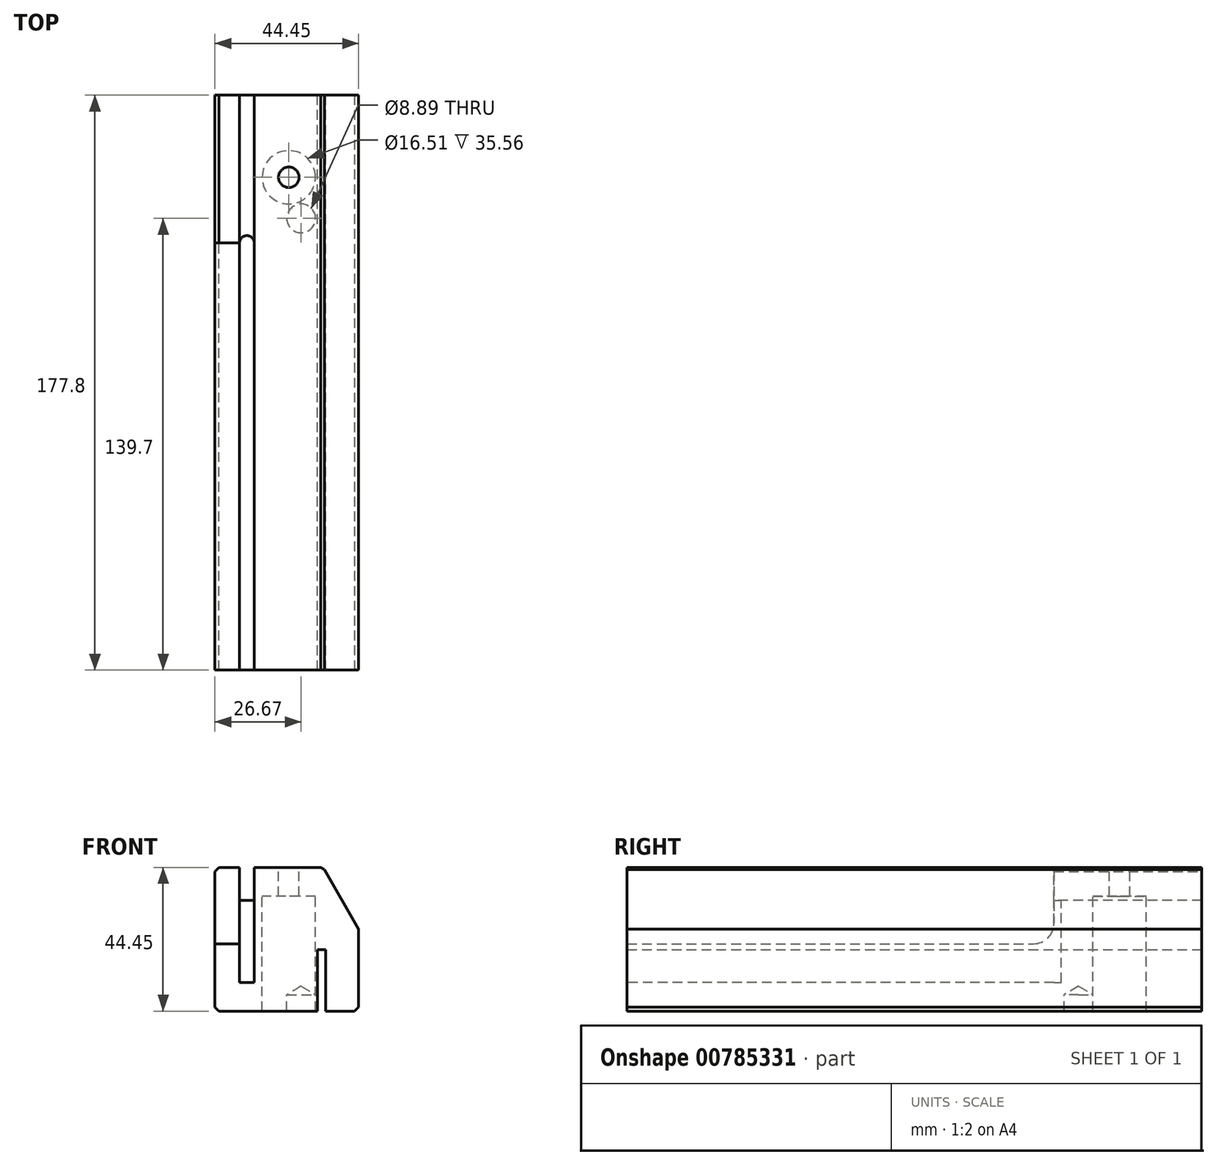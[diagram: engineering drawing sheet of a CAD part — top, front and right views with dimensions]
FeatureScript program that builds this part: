
annotation { "Feature Type Name" : "Feature", "Feature Type Description" : "" }
export const myFeature = defineFeature(function(context is Context, id is Id, definition is map)
    precondition{}
    {
        {
            var Q0;
            Q0=qCreatedBy(makeId("Front.planeOp"),FACE);
            var sketch = newSketch(context, id + "F0", { "sketchPlane" : qUnion([Q0])});
            skLineSegment(sketch, "E0", {"start": v(0, 0) * mm, "end": v(0, 44.45) * mm});
            skLineSegment(sketch, "E1", {"start": v(0, 44.45) * mm, "end": v(33.45, 44.45) * mm});
            skLineSegment(sketch, "E2", {"start": v(33.45, 44.45) * mm, "end": v(44.45, 25.4) * mm});
            skLineSegment(sketch, "E3", {"start": v(44.45, 25.4) * mm, "end": v(44.45, 0) * mm});
            skLineSegment(sketch, "E4.bottom", {"start": v(34.3, 19.05) * mm, "end": v(31.75, 19.05) * mm});
            skLineSegment(sketch, "E4.left", {"start": v(34.3, 19.05) * mm, "end": v(34.3, 0) * mm});
            skLineSegment(sketch, "E4.right", {"start": v(31.75, 19.05) * mm, "end": v(31.75, 0) * mm});
            skLineSegment(sketch, "E5", {"start": v(0, 0) * mm, "end": v(31.75, 0) * mm});
            skLineSegment(sketch, "E6", {"start": v(34.3, 0) * mm, "end": v(44.45, 0) * mm});
            skSolve(sketch);
        }
        {
            var Q0;
            Q0=makeQuery(id+"F0.imprint","IMPRINT",FACE,{"disambiguationData":[TD([[makeQuery(id+"F0.imprint","IMPRINT",EDGE,{"derivedFrom":sQuery(id+"F0.wireOp",EDGE,"E0")}),-1.0]])]});
            extrude(context, id + "F1", {"entities" : qUnion([Q0]), "depth" : 177.8 * mm, "offsetDistance" : 25.4 * mm});
        }
        {
            var Q0;
            Q0=makeQuery(id+"F1.opExtrude","SWEPT_FACE",FACE,{"disambiguationData":[OSD([sQuery(id+"F0.wireOp",EDGE,"E0")])]});
            var sketch = newSketch(context, id + "F2", { "sketchPlane" : qUnion([Q0])});
            skLineSegment(sketch, "E7.bottom", {"start": v(177.8, 44.45) * mm, "end": v(45.72, 44.45) * mm});
            skLineSegment(sketch, "E7.top", {"start": v(177.8, 20.83) * mm, "end": v(52.07, 20.83) * mm});
            skLineSegment(sketch, "E7.left", {"start": v(177.8, 44.45) * mm, "end": v(177.8, 20.83) * mm});
            skLineSegment(sketch, "E7.right", {"start": v(45.72, 44.45) * mm, "end": v(45.72, 27.18) * mm});
            skPoint(sketch, "E8.visualSharp", {"position": v(45.72, 20.83) * mm});
            skArc(sketch, "E8.filletArc", {"start": v(45.72, 27.18) * mm, "mid": v(47.58, 22.69) * mm, "end": v(52.07, 20.83) * mm});
            skSolve(sketch);
        }
        {
            var Q0;
            Q0=makeQuery(id+"F2.imprint","IMPRINT",FACE,{"disambiguationData":[TD([[makeQuery(id+"F2.imprint","IMPRINT",EDGE,{"derivedFrom":sQuery(id+"F2.wireOp",EDGE,"E7.bottom")}),1.0]])]});
            extrude(context, id + "F3", {"entities" : qUnion([Q0]), "operationType" : NewBodyOperationType.REMOVE, "oppositeDirection" : true, "depth" : 9.9 * mm, "offsetDistance" : 25.4 * mm});
        }
        {
            var Q0;
            Q0=makeQuery(id+"F1.opExtrude","SWEPT_FACE",FACE,{"disambiguationData":[OSD([sQuery(id+"F0.wireOp",EDGE,"E1")])]});
            var sketch = newSketch(context, id + "F4", { "sketchPlane" : qUnion([Q0])});
            skLineSegment(sketch, "E9.bottom", {"start": v(7.62, 0) * mm, "end": v(12.2, 0) * mm});
            skLineSegment(sketch, "E9.top", {"start": v(7.62, -177.8) * mm, "end": v(12.2, -177.8) * mm});
            skLineSegment(sketch, "E9.left", {"start": v(7.62, 0) * mm, "end": v(7.62, -177.8) * mm});
            skLineSegment(sketch, "E9.right", {"start": v(12.2, 0) * mm, "end": v(12.2, -177.8) * mm});
            skSolve(sketch);
        }
        {
            var Q0;
            Q0 = qSketchRegion(id + "F4", true);
            extrude(context, id + "F5", {"entities" : qUnion([Q0]), "operationType" : NewBodyOperationType.REMOVE, "oppositeDirection" : true, "depth" : 10.16 * mm, "offsetDistance" : 25.4 * mm});
        }
        {
            var Q0;
            {var subQ6=sQuery(id+"F0.wireOp",EDGE,"E2");var subQ7=sQuery(id+"F0.wireOp",EDGE,"E1");Q0=makeQuery(id+"F5.boolean.opBoolean","SPLIT",FACE,{"disambiguationData":[TD([makeQuery(id+"F1.opExtrude","SWEPT_FACE",FACE,{"disambiguationData":[OSD([subQ6])]})])],"derivedFrom":makeQuery(id+"F1.opExtrude","SWEPT_FACE",FACE,{"disambiguationData":[OSD([subQ7])]})});}
            var sketch = newSketch(context, id + "F6", { "sketchPlane" : qUnion([Q0])});
            skLineSegment(sketch, "E10.top", {"start": v(12.2, -177.8) * mm, "end": v(7.62, -177.8) * mm});
            skLineSegment(sketch, "E10.left", {"start": v(12.2, -45.72) * mm, "end": v(12.2, -177.8) * mm});
            skLineSegment(sketch, "E10.right", {"start": v(7.62, -45.72) * mm, "end": v(7.62, -177.8) * mm});
            skArc(sketch, "E11", {"start": v(12.2, -45.72) * mm, "mid": v(9.9, -43.43) * mm, "end": v(7.62, -45.72) * mm});
            skSolve(sketch);
        }
        {
            var Q0;
            Q0=makeQuery(id+"F6.imprint","IMPRINT",FACE,{"disambiguationData":[TD([[makeQuery(id+"F6.imprint","IMPRINT",EDGE,{"derivedFrom":sQuery(id+"F6.wireOp",EDGE,"E10.top")}),-1.0]])]});
            extrude(context, id + "F7", {"entities" : qUnion([Q0]), "operationType" : NewBodyOperationType.REMOVE, "oppositeDirection" : true, "depth" : 35.56 * mm, "offsetDistance" : 25.4 * mm});
        }
        {
            var Q0;
            Q0=makeQuery(id+"F1.opExtrude","SWEPT_FACE",FACE,{"disambiguationData":[OSD([sQuery(id+"F0.wireOp",EDGE,"E5")])]});
            var sketch = newSketch(context, id + "F8", { "sketchPlane" : qUnion([Q0])});
            skCircle(sketch, "E12", {"center": v(22.86, 25.4) * mm, "radius": 8.26 * mm});
            skCircle(sketch, "E13", {"center": v(26.67, 38.1) * mm, "radius": 4.45 * mm});
            skSolve(sketch);
        }
        {
            var Q0;
            Q0=sQuery(id+"F8.wireOp",VERTEX,"E13.center");
            var Q1;
            Q1=makeQuery(id+"F1.opExtrude","SWEPT_BODY",BODY,{"disambiguationData":[OSD([sQuery(id+"F0.wireOp",EDGE,"E0"),sQuery(id+"F0.wireOp",EDGE,"E1"),sQuery(id+"F0.wireOp",EDGE,"E2"),sQuery(id+"F0.wireOp",EDGE,"E3"),sQuery(id+"F0.wireOp",EDGE,"E4.bottom"),sQuery(id+"F0.wireOp",EDGE,"E4.left"),sQuery(id+"F0.wireOp",EDGE,"E4.right"),sQuery(id+"F0.wireOp",EDGE,"E5"),sQuery(id+"F0.wireOp",EDGE,"E6")])]});
            hole(context, id + "F9", {"style" : HoleStyle.SIMPLE, "endStyle" : HoleEndStyle.BLIND, "holeDiameter" : 8.9 * mm, "majorDiameter" : 6.35 * mm, "holeDepth" : 5.08 * mm, "isTappedThrough" : true, "tappedDepth" : 12.7 * mm, "tapClearance" : 3, "startFromSketch" : true, "locations" : qUnion([Q0]), "scope" : qUnion([Q1])});
        }
        {
            var Q0;
            Q0=sQuery(id+"F8.wireOp",VERTEX,"E12.center");
            var Q1;
            Q1=makeQuery(id+"F1.opExtrude","SWEPT_BODY",BODY,{"disambiguationData":[OSD([sQuery(id+"F0.wireOp",EDGE,"E0"),sQuery(id+"F0.wireOp",EDGE,"E1"),sQuery(id+"F0.wireOp",EDGE,"E2"),sQuery(id+"F0.wireOp",EDGE,"E3"),sQuery(id+"F0.wireOp",EDGE,"E4.bottom"),sQuery(id+"F0.wireOp",EDGE,"E4.left"),sQuery(id+"F0.wireOp",EDGE,"E4.right"),sQuery(id+"F0.wireOp",EDGE,"E5"),sQuery(id+"F0.wireOp",EDGE,"E6")])]});
            hole(context, id + "F10", {"style" : HoleStyle.C_BORE, "endStyle" : HoleEndStyle.THROUGH, "holeDiameter" : 6.35 * mm, "cBoreDiameter" : 16.5 * mm, "cBoreDepth" : 35.56 * mm, "majorDiameter" : 6.35 * mm, "isTappedThrough" : true, "tappedDepth" : 12.7 * mm, "tapClearance" : 3, "startFromSketch" : true, "locations" : qUnion([Q0]), "scope" : qUnion([Q1])});
        }
        {
            var Q0;
            Q0=makeQuery(id+"F5.boolean.opBoolean","COPY",EDGE,{"derivedFrom":makeQuery(id+"F5.opExtrude","CAP_EDGE",EDGE,{"disambiguationData":[OSD([sQuery(id+"F4.wireOp",EDGE,"E9.right")])],"isStart":true})});
            var Q1;
            Q1=makeQuery(id+"F5.boolean.opBoolean","COPY",EDGE,{"derivedFrom":makeQuery(id+"F5.opExtrude","CAP_EDGE",EDGE,{"disambiguationData":[OSD([sQuery(id+"F4.wireOp",EDGE,"E9.left")])],"isStart":true})});
            var Q2;
            Q2=makeQuery(id+"F1.opExtrude","SWEPT_EDGE",EDGE,{"disambiguationData":[OSD([sQuery(id+"F0.wireOp",EDGE,"E0"),sQuery(id+"F0.wireOp",EDGE,"E1")])]});
            var Q3;
            Q3=makeQuery(id+"F1.opExtrude","SWEPT_EDGE",EDGE,{"disambiguationData":[OSD([sQuery(id+"F0.wireOp",EDGE,"E0"),sQuery(id+"F0.wireOp",EDGE,"E5")])]});
            var Q4;
            Q4=makeQuery(id+"F1.opExtrude","SWEPT_EDGE",EDGE,{"disambiguationData":[OSD([sQuery(id+"F0.wireOp",EDGE,"E3"),sQuery(id+"F0.wireOp",EDGE,"E6")])]});
            var Q5;
            Q5=makeQuery(id+"F1.opExtrude","SWEPT_EDGE",EDGE,{"disambiguationData":[OSD([sQuery(id+"F0.wireOp",EDGE,"E1"),sQuery(id+"F0.wireOp",EDGE,"E2")])]});
            chamfer(context, id + "F11", {"entities" : qUnion([Q0, Q1, Q2, Q3, Q4, Q5]), "width" : 1.27 * mm, "tangentPropagation" : true});
        }
    });
